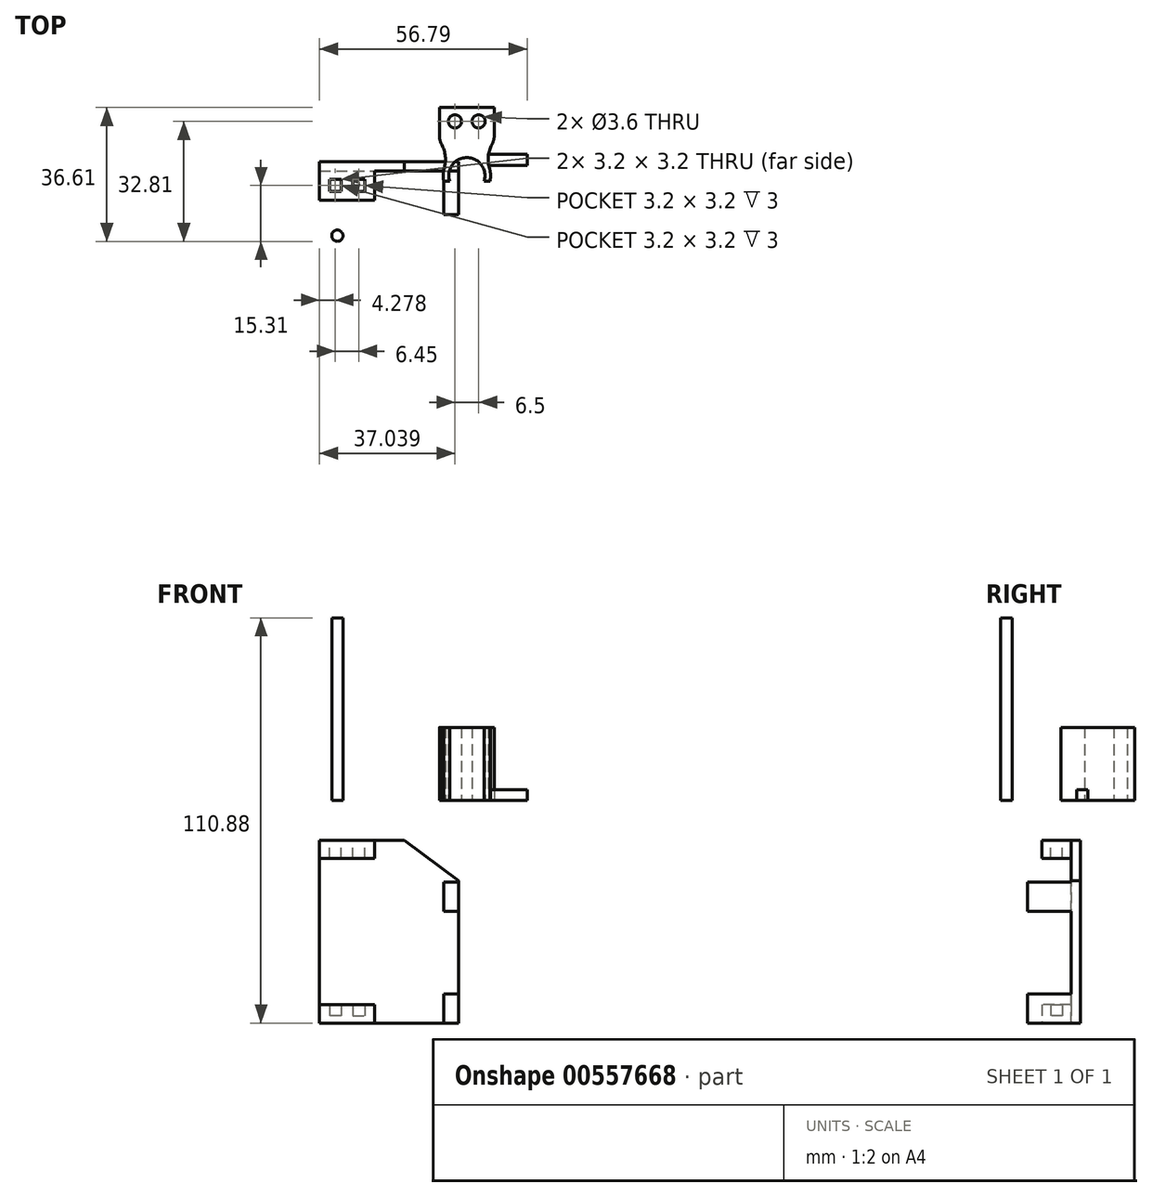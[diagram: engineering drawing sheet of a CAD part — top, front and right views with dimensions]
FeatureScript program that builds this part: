
annotation { "Feature Type Name" : "Feature", "Feature Type Description" : "" }
export const myFeature = defineFeature(function(context is Context, id is Id, definition is map)
    precondition{}
    {
        {
            var Q0;
            Q0=qCreatedBy(makeId("Top.planeOp"),FACE);
            var sketch = newSketch(context, id + "F0", { "sketchPlane" : qUnion([Q0])});
            skLineSegment(sketch, "E0.bottom", {"start": v(-16.7, 14.85) * mm, "end": v(-1.7, 14.85) * mm});
            skLineSegment(sketch, "E0.left", {"start": v(-16.7, 14.85) * mm, "end": v(-16.7, 7.14) * mm});
            skLineSegment(sketch, "E0.right", {"start": v(-1.7, 14.85) * mm, "end": v(-1.7, 7.14) * mm});
            skLineSegment(sketch, "E1", {"start": v(-9.2, 14.85) * mm, "end": v(-9.2, -3.8) * mm, "construction": true});
            skArc(sketch, "E2", {"start": v(-4.48, -5.28) * mm, "mid": v(-9.2, 1.15) * mm, "end": v(-13.92, -5.28) * mm});
            skArc(sketch, "E3", {"start": v(-15.41, -1.88) * mm, "mid": v(-15.7, -3.57) * mm, "end": v(-15.53, -5.28) * mm});
            skArc(sketch, "E4", {"start": v(-15.41, -1.88) * mm, "mid": v(-15.08, 1.5) * mm, "end": v(-16.08, 4.73) * mm});
            skPoint(sketch, "E5.visualSharp", {"position": v(-16.7, 5.7) * mm});
            skArc(sketch, "E5.filletArc", {"start": v(-16.7, 7.14) * mm, "mid": v(-16.54, 5.9) * mm, "end": v(-16.08, 4.73) * mm});
            skArc(sketch, "E6.MirrorCS", {"start": v(-3, -1.88) * mm, "mid": v(-3.33, 1.5) * mm, "end": v(-2.32, 4.73) * mm});
            skArc(sketch, "E7.MirrorCS", {"start": v(-1.7, 7.14) * mm, "mid": v(-1.86, 5.9) * mm, "end": v(-2.32, 4.73) * mm});
            skLineSegment(sketch, "E8", {"start": v(-13.11, -5.28) * mm, "end": v(3.04, -5.28) * mm, "construction": true});
            skArc(sketch, "E9.trimOffspring", {"start": v(-2.87, -5.28) * mm, "mid": v(-2.7, -3.57) * mm, "end": v(-3, -1.88) * mm});
            skLineSegment(sketch, "E10", {"start": v(-15.53, -5.28) * mm, "end": v(-13.92, -5.28) * mm});
            skLineSegment(sketch, "E11", {"start": v(-4.48, -5.28) * mm, "end": v(-2.87, -5.28) * mm});
            skLineSegment(sketch, "E12.bottom", {"start": v(-14.35, 9.05) * mm, "end": v(-10.55, 9.05) * mm, "construction": true});
            skLineSegment(sketch, "E12.top", {"start": v(-14.35, 12.85) * mm, "end": v(-10.55, 12.85) * mm, "construction": true});
            skLineSegment(sketch, "E12.left", {"start": v(-14.35, 9.05) * mm, "end": v(-14.35, 12.85) * mm, "construction": true});
            skLineSegment(sketch, "E12.right", {"start": v(-10.55, 9.05) * mm, "end": v(-10.55, 12.85) * mm, "construction": true});
            skLineSegment(sketch, "E13.MirrorCS", {"start": v(-7.85, 9.05) * mm, "end": v(-7.85, 12.85) * mm, "construction": true});
            skLineSegment(sketch, "E14.MirrorCS", {"start": v(-4.05, 12.85) * mm, "end": v(-7.85, 12.85) * mm, "construction": true});
            skLineSegment(sketch, "E15.MirrorCS", {"start": v(-4.05, 9.05) * mm, "end": v(-4.05, 12.85) * mm, "construction": true});
            skLineSegment(sketch, "E16.MirrorCS", {"start": v(-4.05, 9.05) * mm, "end": v(-7.85, 9.05) * mm, "construction": true});
            skLineSegment(sketch, "E17", {"start": v(-12.45, 9.05) * mm, "end": v(-12.45, 14.07) * mm, "construction": true});
            skLineSegment(sketch, "E18", {"start": v(-5.95, 9.05) * mm, "end": v(-5.95, 13.68) * mm, "construction": true});
            skPoint(sketch, "E18.endSnap0", {"position": v(-5.95, 12.85) * mm});
            skLineSegment(sketch, "E19", {"start": v(-10.55, 10.95) * mm, "end": v(-10.55, 10.95) * mm});
            skPoint(sketch, "E19.endSnap0", {"position": v(-14.35, 10.95) * mm});
            skCircle(sketch, "E20", {"center": v(-12.45, 11.05) * mm, "radius": 1.8 * mm});
            skCircle(sketch, "E21", {"center": v(-5.95, 11.05) * mm, "radius": 1.8 * mm});
            skSolve(sketch);
        }
        {
            var Q0;
            Q0=makeQuery(id+"F0.imprint","IMPRINT",FACE,{"disambiguationData":[TD([[makeQuery(id+"F0.imprint","IMPRINT",EDGE,{"derivedFrom":sQuery(id+"F0.wireOp",EDGE,"E0.bottom")}),-1.0]])]});
            extrude(context, id + "F1", {"entities" : qUnion([Q0]), "depth" : 20 * mm, "offsetDistance" : 25 * mm});
        }
        {
            var Q0;
            Q0=qCreatedBy(makeId("Top.planeOp"),FACE);
            var sketch = newSketch(context, id + "F2", { "sketchPlane" : qUnion([Q0])});
            skCircle(sketch, "E22", {"center": v(-44.63, -20.21) * mm, "radius": 1.55 * mm});
            skSolve(sketch);
        }
        {
            var Q0;
            Q0=makeQuery(id+"F2.imprint","IMPRINT",FACE,{"disambiguationData":[TD([[makeQuery(id+"F2.imprint","IMPRINT",EDGE,{"derivedFrom":sQuery(id+"F2.wireOp",EDGE,"E22")}),1.0]])]});
            extrude(context, id + "F3", {"entities" : qUnion([Q0]), "depth" : 50 * mm, "offsetDistance" : 25 * mm});
        }
        {
            var Q0;
            Q0=qCreatedBy(makeId("Front.planeOp"),FACE);
            var sketch = newSketch(context, id + "F4", { "sketchPlane" : qUnion([Q0])});
            skLineSegment(sketch, "E23.bottom", {"start": v(-49.49, -10.88) * mm, "end": v(-26.31, -10.88) * mm});
            skLineSegment(sketch, "E23.top", {"start": v(-49.49, -60.88) * mm, "end": v(-11.49, -60.88) * mm});
            skLineSegment(sketch, "E23.left", {"start": v(-49.49, -10.88) * mm, "end": v(-49.49, -60.88) * mm});
            skLineSegment(sketch, "E23.right", {"start": v(-11.49, -21.9) * mm, "end": v(-11.49, -60.88) * mm});
            skLineSegment(sketch, "E24", {"start": v(-26.31, -10.88) * mm, "end": v(-11.49, -21.9) * mm});
            skPoint(sketch, "E25.orphan", {"position": v(-11.49, -10.88) * mm});
            skSolve(sketch);
        }
        {
            var Q0;
            Q0=qSketchRegion(id+"F4",true);
            extrude(context, id + "F5", {"entities" : qUnion([Q0]), "depth" : 2.5 * mm, "offsetDistance" : 25 * mm});
        }
        {
            var Q0;
            Q0=makeQuery(id+"F5.opExtrude","SWEPT_FACE",FACE,{"disambiguationData":[OSD([sQuery(id+"F4.wireOp",EDGE,"E23.bottom")])]});
            cPlane(context, id + "F6", {"entities" : qUnion([Q0]), "cplaneType" : CPlaneType.OFFSET, "offset" : 0 * mm, "width" : 150 * mm, "height" : 150 * mm});
        }
        {
            var Q0;
            Q0=qCreatedBy(id+"F6.planeOp",FACE);
            var sketch = newSketch(context, id + "F7", { "sketchPlane" : qUnion([Q0])});
            skLineSegment(sketch, "E26.bottom", {"start": v(-49.49, -2.5) * mm, "end": v(-34.49, -2.5) * mm});
            skLineSegment(sketch, "E26.top", {"start": v(-49.49, -10.5) * mm, "end": v(-34.49, -10.5) * mm});
            skLineSegment(sketch, "E26.left", {"start": v(-49.49, -2.5) * mm, "end": v(-49.49, -10.5) * mm});
            skLineSegment(sketch, "E26.right", {"start": v(-34.49, -2.5) * mm, "end": v(-34.49, -10.5) * mm});
            skLineSegment(sketch, "E27.bottom", {"start": v(-40.36, -4.85) * mm, "end": v(-37.16, -4.85) * mm});
            skLineSegment(sketch, "E27.top", {"start": v(-40.36, -8.05) * mm, "end": v(-37.16, -8.05) * mm});
            skLineSegment(sketch, "E27.left", {"start": v(-40.36, -4.85) * mm, "end": v(-40.36, -8.05) * mm});
            skLineSegment(sketch, "E27.right", {"start": v(-37.16, -4.85) * mm, "end": v(-37.16, -8.05) * mm});
            skLineSegment(sketch, "E28", {"start": v(-41.99, -2.5) * mm, "end": v(-41.99, -10.5) * mm, "construction": true});
            skLineSegment(sketch, "E29.MirrorCS", {"start": v(-43.61, -4.85) * mm, "end": v(-43.61, -8.05) * mm});
            skLineSegment(sketch, "E30.MirrorCS", {"start": v(-43.61, -8.05) * mm, "end": v(-46.81, -8.05) * mm});
            skLineSegment(sketch, "E31.MirrorCS", {"start": v(-46.81, -4.85) * mm, "end": v(-46.81, -8.05) * mm});
            skLineSegment(sketch, "E32.MirrorCS", {"start": v(-43.61, -4.85) * mm, "end": v(-46.81, -4.85) * mm});
            skLineSegment(sketch, "E33", {"start": v(-45.21, -4.85) * mm, "end": v(-45.21, -8.05) * mm, "construction": true});
            skLineSegment(sketch, "E34", {"start": v(-38.76, -4.85) * mm, "end": v(-38.76, -8.05) * mm, "construction": true});
            skSolve(sketch);
        }
        {
            var Q0;
            Q0=qSketchRegion(id+"F7",true);
            extrude(context, id + "F8", {"entities" : qUnion([Q0]), "operationType" : NewBodyOperationType.ADD, "oppositeDirection" : true, "depth" : 5 * mm, "offsetDistance" : 25 * mm});
        }
        {
            var Q0;
            Q0=makeQuery(id+"F5.opExtrude","SWEPT_FACE",FACE,{"disambiguationData":[OSD([sQuery(id+"F4.wireOp",EDGE,"E23.top")])]});
            cPlane(context, id + "F9", {"entities" : qUnion([Q0]), "cplaneType" : CPlaneType.OFFSET, "offset" : 0 * mm, "width" : 150 * mm, "height" : 150 * mm});
        }
        {
            var Q0;
            Q0=qCreatedBy(id+"F9.planeOp",FACE);
            var sketch = newSketch(context, id + "F10", { "sketchPlane" : qUnion([Q0])});
            skLineSegment(sketch, "E35.bottom", {"start": v(-49.49, 2.5) * mm, "end": v(-34.49, 2.5) * mm});
            skLineSegment(sketch, "E35.top", {"start": v(-49.49, 10.5) * mm, "end": v(-34.49, 10.5) * mm});
            skLineSegment(sketch, "E35.left", {"start": v(-49.49, 2.5) * mm, "end": v(-49.49, 10.5) * mm});
            skLineSegment(sketch, "E35.right", {"start": v(-34.49, 2.5) * mm, "end": v(-34.49, 10.5) * mm});
            skLineSegment(sketch, "E36.bottom", {"start": v(-46.81, 8.05) * mm, "end": v(-43.61, 8.05) * mm});
            skLineSegment(sketch, "E36.top", {"start": v(-46.81, 4.85) * mm, "end": v(-43.61, 4.85) * mm});
            skLineSegment(sketch, "E36.left", {"start": v(-46.81, 8.05) * mm, "end": v(-46.81, 4.85) * mm});
            skLineSegment(sketch, "E36.right", {"start": v(-43.61, 8.05) * mm, "end": v(-43.61, 4.85) * mm});
            skLineSegment(sketch, "E37", {"start": v(-41.99, 2.5) * mm, "end": v(-41.99, 10.5) * mm, "construction": true});
            skLineSegment(sketch, "E38.MirrorCS", {"start": v(-40.36, 8.05) * mm, "end": v(-40.36, 4.85) * mm});
            skLineSegment(sketch, "E39.MirrorCS", {"start": v(-37.16, 8.05) * mm, "end": v(-40.36, 8.05) * mm});
            skLineSegment(sketch, "E40.MirrorCS", {"start": v(-37.16, 4.85) * mm, "end": v(-40.36, 4.85) * mm});
            skLineSegment(sketch, "E41.MirrorCS", {"start": v(-37.16, 8.05) * mm, "end": v(-37.16, 4.85) * mm});
            skLineSegment(sketch, "E42", {"start": v(-45.21, 4.85) * mm, "end": v(-45.21, 8.05) * mm, "construction": true});
            skLineSegment(sketch, "E43", {"start": v(-38.76, 4.85) * mm, "end": v(-38.76, 8.05) * mm, "construction": true});
            skSolve(sketch);
        }
        {
            var Q0;
            Q0=makeQuery(id+"F10.imprint","IMPRINT",FACE,{"disambiguationData":[TD([[makeQuery(id+"F10.imprint","IMPRINT",EDGE,{"derivedFrom":sQuery(id+"F10.wireOp",EDGE,"E35.bottom")}),1.0]])]});
            extrude(context, id + "F11", {"entities" : qUnion([Q0]), "operationType" : NewBodyOperationType.ADD, "oppositeDirection" : true, "depth" : 5 * mm, "offsetDistance" : 25 * mm});
        }
        {
            var Q0;
            Q0=qSketchRegion(id+"F7",true);
            var Q1;
            Q1=makeQuery(id+"F8.boolean.opBoolean","MERGE",FACE,{"derivedFrom":[makeQuery(id+"F5.opExtrude","SWEPT_FACE",FACE,{"disambiguationData":[OSD([sQuery(id+"F4.wireOp",EDGE,"E23.bottom")])]}),makeQuery(id+"F8.opExtrude","CAP_FACE",FACE,{"disambiguationData":[OSD([sQuery(id+"F7.wireOp",EDGE,"E26.bottom"),sQuery(id+"F7.wireOp",EDGE,"E26.top"),sQuery(id+"F7.wireOp",EDGE,"E26.left"),sQuery(id+"F7.wireOp",EDGE,"E26.right"),sQuery(id+"F7.wireOp",EDGE,"E27.bottom"),sQuery(id+"F7.wireOp",EDGE,"E27.top"),sQuery(id+"F7.wireOp",EDGE,"E27.left"),sQuery(id+"F7.wireOp",EDGE,"E27.right"),sQuery(id+"F7.wireOp",EDGE,"E29.MirrorCS"),sQuery(id+"F7.wireOp",EDGE,"E30.MirrorCS"),sQuery(id+"F7.wireOp",EDGE,"E31.MirrorCS"),sQuery(id+"F7.wireOp",EDGE,"E32.MirrorCS")])],"isStart":true})]});
            extrude(context, id + "F12", {"entities" : qUnion([Q0, Q1]), "operationType" : NewBodyOperationType.ADD, "oppositeDirection" : true, "depth" : 5 * mm, "offsetDistance" : 25 * mm});
        }
        {
            var Q0;
            Q0=qSketchRegion(id+"F10",true);
            extrude(context, id + "F13", {"entities" : qUnion([Q0]), "operationType" : NewBodyOperationType.ADD, "oppositeDirection" : true, "depth" : 5 * mm, "offsetDistance" : 25 * mm});
        }
        {
            var Q0;
            Q0=makeQuery(id+"F11.boolean.opBoolean","MERGE",FACE,{"derivedFrom":[makeQuery(id+"F5.opExtrude","SWEPT_FACE",FACE,{"disambiguationData":[OSD([sQuery(id+"F4.wireOp",EDGE,"E23.top")])]}),makeQuery(id+"F11.opExtrude","CAP_FACE",FACE,{"disambiguationData":[OSD([sQuery(id+"F10.wireOp",EDGE,"E35.bottom"),sQuery(id+"F10.wireOp",EDGE,"E35.top"),sQuery(id+"F10.wireOp",EDGE,"E35.left"),sQuery(id+"F10.wireOp",EDGE,"E35.right"),sQuery(id+"F10.wireOp",EDGE,"E36.bottom"),sQuery(id+"F10.wireOp",EDGE,"E36.top"),sQuery(id+"F10.wireOp",EDGE,"E36.left"),sQuery(id+"F10.wireOp",EDGE,"E36.right"),sQuery(id+"F10.wireOp",EDGE,"E38.MirrorCS"),sQuery(id+"F10.wireOp",EDGE,"E39.MirrorCS"),sQuery(id+"F10.wireOp",EDGE,"E40.MirrorCS"),sQuery(id+"F10.wireOp",EDGE,"E41.MirrorCS")])],"isStart":true})]});
            cPlane(context, id + "F14", {"entities" : qUnion([Q0]), "cplaneType" : CPlaneType.OFFSET, "offset" : 0 * mm, "width" : 150 * mm, "height" : 150 * mm});
        }
        {
            var Q0;
            Q0=qCreatedBy(id+"F14.planeOp",FACE);
            var sketch = newSketch(context, id + "F15", { "sketchPlane" : qUnion([Q0])});
            skLineSegment(sketch, "E44.bottom", {"start": v(-40.36, 8.05) * mm, "end": v(-36.86, 8.05) * mm});
            skLineSegment(sketch, "E44.top", {"start": v(-40.36, 4.55) * mm, "end": v(-36.86, 4.55) * mm});
            skLineSegment(sketch, "E44.left", {"start": v(-40.36, 8.05) * mm, "end": v(-40.36, 4.55) * mm});
            skLineSegment(sketch, "E44.right", {"start": v(-36.86, 8.05) * mm, "end": v(-36.86, 4.55) * mm});
            skLineSegment(sketch, "E45.bottom", {"start": v(-43.31, 4.85) * mm, "end": v(-46.81, 4.85) * mm});
            skLineSegment(sketch, "E45.top", {"start": v(-43.31, 8.35) * mm, "end": v(-46.81, 8.35) * mm});
            skLineSegment(sketch, "E45.left", {"start": v(-43.31, 4.85) * mm, "end": v(-43.31, 8.35) * mm});
            skLineSegment(sketch, "E45.right", {"start": v(-46.81, 4.85) * mm, "end": v(-46.81, 8.35) * mm});
            skSolve(sketch);
        }
        {
            var Q0;
            Q0=qSketchRegion(id+"F15",true);
            extrude(context, id + "F16", {"entities" : qUnion([Q0]), "operationType" : NewBodyOperationType.ADD, "oppositeDirection" : true, "depth" : 2 * mm, "offsetDistance" : 25 * mm});
        }
        {
            var Q0;
            Q0=makeQuery(id+"F1.opExtrude","SWEPT_FACE",FACE,{"disambiguationData":[OSD([sQuery(id+"F0.wireOp",EDGE,"E0.right")])]});
            cPlane(context, id + "F17", {"entities" : qUnion([Q0]), "cplaneType" : CPlaneType.OFFSET, "offset" : 9 * mm, "width" : 150 * mm, "height" : 150 * mm});
        }
        {
            var Q0;
            Q0=qCreatedBy(id+"F17.planeOp",FACE);
            var sketch = newSketch(context, id + "F18", { "sketchPlane" : qUnion([Q0])});
            skLineSegment(sketch, "E46", {"start": v(-0.93, 0) * mm, "end": v(1.52, 0) * mm});
            skLineSegment(sketch, "E47.bottom", {"start": v(-0.93, 0) * mm, "end": v(2.07, 0) * mm});
            skLineSegment(sketch, "E47.top", {"start": v(-0.93, 3) * mm, "end": v(2.07, 3) * mm});
            skLineSegment(sketch, "E47.left", {"start": v(-0.93, 0) * mm, "end": v(-0.93, 3) * mm});
            skLineSegment(sketch, "E47.right", {"start": v(2.07, 0) * mm, "end": v(2.07, 3) * mm});
            skSolve(sketch);
        }
        {
            var Q0;
            Q0=qSketchRegion(id+"F18",true);
            var Q1;
            Q1=qCreatedBy(id+"F17.planeOp",FACE);
            extrude(context, id + "F19", {"entities" : qUnion([Q0]), "operationType" : NewBodyOperationType.ADD, "endBound" : BoundingType.UP_TO_NEXT, "oppositeDirection" : true, "depth" : 25 * mm, "endBoundEntityFace" : qUnion([Q1]), "offsetDistance" : 25 * mm});
        }
        {
            var Q0;
            Q0=makeQuery(id+"F5.opExtrude","CAP_FACE",FACE,{"disambiguationData":[OSD([sQuery(id+"F4.wireOp",EDGE,"E23.bottom"),sQuery(id+"F4.wireOp",EDGE,"E23.top"),sQuery(id+"F4.wireOp",EDGE,"E23.left"),sQuery(id+"F4.wireOp",EDGE,"E23.right")])],"isStart":false});
            cPlane(context, id + "F20", {"entities" : qUnion([Q0]), "cplaneType" : CPlaneType.OFFSET, "offset" : 0 * mm, "width" : 150 * mm, "height" : 150 * mm});
        }
        {
            var Q0;
            Q0=qCreatedBy(id+"F20.planeOp",FACE);
            var sketch = newSketch(context, id + "F21", { "sketchPlane" : qUnion([Q0])});
            skLineSegment(sketch, "E48.bottom", {"start": v(-11.49, -60.88) * mm, "end": v(-15.49, -60.88) * mm});
            skLineSegment(sketch, "E48.top", {"start": v(-11.49, -52.88) * mm, "end": v(-15.49, -52.88) * mm});
            skLineSegment(sketch, "E48.left", {"start": v(-11.49, -60.88) * mm, "end": v(-11.49, -52.88) * mm});
            skLineSegment(sketch, "E48.right", {"start": v(-15.49, -60.88) * mm, "end": v(-15.49, -52.88) * mm});
            skLineSegment(sketch, "E49", {"start": v(-15.49, -52.88) * mm, "end": v(-15.49, -30.35) * mm, "construction": true});
            skLineSegment(sketch, "E50.bottom", {"start": v(-15.49, -30.35) * mm, "end": v(-11.49, -30.35) * mm});
            skLineSegment(sketch, "E50.top", {"start": v(-15.49, -22.35) * mm, "end": v(-11.49, -22.35) * mm});
            skLineSegment(sketch, "E50.left", {"start": v(-15.49, -30.35) * mm, "end": v(-15.49, -22.35) * mm});
            skLineSegment(sketch, "E50.right", {"start": v(-11.49, -30.35) * mm, "end": v(-11.49, -22.35) * mm});
            skSolve(sketch);
        }
        {
            var Q0;
            Q0=qSketchRegion(id+"F21",true);
            extrude(context, id + "F22", {"entities" : qUnion([Q0]), "operationType" : NewBodyOperationType.ADD, "depth" : 12 * mm, "offsetDistance" : 25 * mm});
        }
    });
